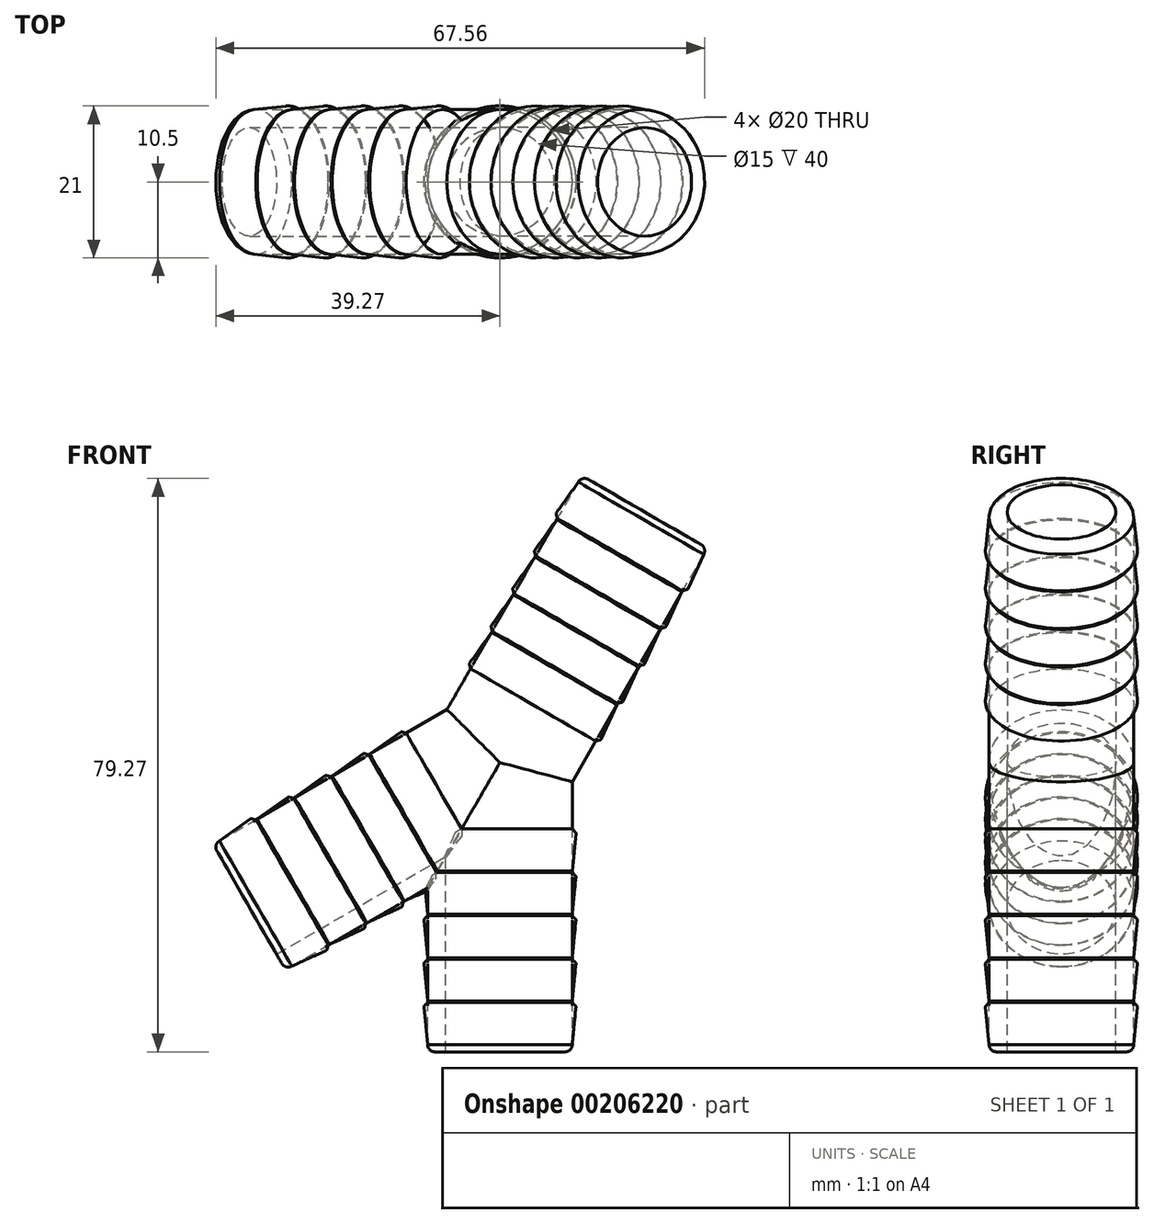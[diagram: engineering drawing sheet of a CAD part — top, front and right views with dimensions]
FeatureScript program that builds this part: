
annotation { "Feature Type Name" : "Feature", "Feature Type Description" : "" }
export const myFeature = defineFeature(function(context is Context, id is Id, definition is map)
    precondition{}
    {
        {
            var Q0;
            Q0=qCreatedBy(makeId("Front.planeOp"),FACE);
            var sketch = newSketch(context, id + "F4", { "sketchPlane" : qUnion([Q0])});
            skLineSegment(sketch, "E0.bottom", {"start": v(-10, 0) * mm, "end": v(10, 0) * mm});
            skLineSegment(sketch, "E0.top", {"start": v(-9, -40) * mm, "end": v(9, -40) * mm});
            skLineSegment(sketch, "E0.left", {"start": v(-10, 0) * mm, "end": v(-10, -39) * mm});
            skLineSegment(sketch, "E0.right", {"start": v(10, 0) * mm, "end": v(10, -39) * mm});
            skCircle(sketch, "E1", {"center": v(0, 0) * mm, "radius": 10 * mm});
            skLineSegment(sketch, "E2", {"start": v(0, 0) * mm, "end": v(0, -82.88) * mm});
            skPoint(sketch, "E3.visualSharp", {"position": v(-10, -40) * mm});
            skArc(sketch, "E3.filletArc", {"start": v(-10, -39) * mm, "mid": v(-9.7, -39.7) * mm, "end": v(-9, -40) * mm});
            skPoint(sketch, "E4.visualSharp", {"position": v(10, -40) * mm});
            skArc(sketch, "E4.filletArc", {"start": v(9, -40) * mm, "mid": v(9.7, -39.7) * mm, "end": v(10, -39) * mm});
            skArc(sketch, "E5", {"start": v(-10.43, -33.62) * mm, "mid": v(-10.49, -33.71) * mm, "end": v(-10.5, -33.82) * mm});
            skLineSegment(sketch, "E6", {"start": v(-10.5, -33.82) * mm, "end": v(-10, -39) * mm});
            skLineSegment(sketch, "E7", {"start": v(-10.43, -33.62) * mm, "end": v(-10, -33.2) * mm});
            skLineSegment(sketch, "E8.0.1.0", {"start": v(-10.43, -27.62) * mm, "end": v(-10, -27.2) * mm});
            skArc(sketch, "E8.0.1.1", {"start": v(-10.43, -27.62) * mm, "mid": v(-10.49, -27.71) * mm, "end": v(-10.5, -27.82) * mm});
            skLineSegment(sketch, "E8.0.1.2", {"start": v(-10.5, -27.82) * mm, "end": v(-10, -33) * mm});
            skLineSegment(sketch, "E8.0.2.0", {"start": v(-10.43, -21.62) * mm, "end": v(-10, -21.2) * mm});
            skArc(sketch, "E8.0.2.1", {"start": v(-10.43, -21.62) * mm, "mid": v(-10.49, -21.71) * mm, "end": v(-10.5, -21.82) * mm});
            skLineSegment(sketch, "E8.0.2.2", {"start": v(-10.5, -21.82) * mm, "end": v(-10, -27) * mm});
            skLineSegment(sketch, "E8.0.3.0", {"start": v(-10.43, -15.62) * mm, "end": v(-10, -15.2) * mm});
            skArc(sketch, "E8.0.3.1", {"start": v(-10.43, -15.62) * mm, "mid": v(-10.49, -15.71) * mm, "end": v(-10.5, -15.82) * mm});
            skLineSegment(sketch, "E8.0.3.2", {"start": v(-10.5, -15.82) * mm, "end": v(-10, -21) * mm});
            skLineSegment(sketch, "E8.0.4.0", {"start": v(-10.43, -9.62) * mm, "end": v(-10, -9.2) * mm});
            skArc(sketch, "E8.0.4.1", {"start": v(-10.43, -9.62) * mm, "mid": v(-10.49, -9.71) * mm, "end": v(-10.5, -9.82) * mm});
            skLineSegment(sketch, "E8.0.4.2", {"start": v(-10.5, -9.82) * mm, "end": v(-10, -15) * mm});
            skLineSegment(sketch, "E8.direction1", {"start": v(-10.5, -33.82) * mm, "end": v(14.5, -33.82) * mm, "construction": true});
            skLineSegment(sketch, "E8.direction2", {"start": v(-10.5, -33.82) * mm, "end": v(-10.5, -27.82) * mm, "construction": true});
            skSolve(sketch);
        }
        {
            var Q0;
            {var subQ11=sQuery(id+"F4.wireOp",EDGE,"E3.filletArc");Q0=makeQuery(id+"F4.imprint","IMPRINT",FACE,{"disambiguationData":[TD([[makeQuery(id+"F4.imprint","IMPRINT",EDGE,{"derivedFrom":subQ11}),1.0]])]});}
            var Q1;
            {var subQ1=sQuery(id+"F4.wireOp",EDGE,"E0.bottom");var subQ3=sQuery(id+"F4.wireOp",EDGE,"E2");var subQ4=makeQuery(id+"F4.imprint","INTERSECT",VERTEX,{"derivedFrom":[subQ1,subQ3]});Q1=makeQuery(id+"F4.imprint","IMPRINT",FACE,{"disambiguationData":[TD([[makeQuery(id+"F4.imprint","IMPRINT",EDGE,{"disambiguationData":[TD([[subQ4,-1.0]])],"derivedFrom":subQ3}),-1.0]])]});}
            var Q2;
            Q2=sQuery(id+"F4.wireOp",EDGE,"E2");
            revolve(context, id + "F0", {"entities" : qUnion([Q0, Q1]), "axis" : qUnion([Q2]), "revolveType" : RevolveType.FULL});
        }
        {
            var Q0;
            Q0=makeQuery(id+"F6e7yGGuFcoaENt3P_0.opExtrude","SWEPT_BODY",BODY,{"disambiguationData":[OSD([sQuery(id+"F4.wireOp",EDGE,"E0.bottom"),sQuery(id+"F4.wireOp",EDGE,"E0.top"),sQuery(id+"F4.wireOp",EDGE,"E0.left"),sQuery(id+"F4.wireOp",EDGE,"E0.right")])]});
            var Q1;
            Q1=makeQuery(id+"F0.opRevolve","SWEPT_BODY",BODY,{"disambiguationData":[OSD([sQuery(id+"F4.wireOp",EDGE,"E0.bottom"),sQuery(id+"F4.wireOp",EDGE,"E0.top"),sQuery(id+"F4.wireOp",EDGE,"E0.left"),sQuery(id+"F4.wireOp",EDGE,"E2")])]});
            var Q2;
            Q2=sQuery(id+"F4.wireOp",EDGE,"E1");
            circularPattern(context, id + "F1", {"operationType" : NewBodyOperationType.ADD, "entities" : qUnion([Q0, Q1]), "axis" : qUnion([Q2]), "angle" : 300 * degree, "instanceCount" : 3, "equalSpace" : true});
        }
        {
            var Q0;
            {var subQ0=sQuery(id+"F4.wireOp",EDGE,"E8.0.4.0");Q0=makeQuery(id+"F4.imprint","IMPRINT",FACE,{"disambiguationData":[TD([[makeQuery(id+"F4.imprint","IMPRINT",EDGE,{"derivedFrom":subQ0}),-1.0]])]});}
            var Q1;
            {var subQ0=sQuery(id+"F4.wireOp",EDGE,"E8.0.3.0");Q1=makeQuery(id+"F4.imprint","IMPRINT",FACE,{"disambiguationData":[TD([[makeQuery(id+"F4.imprint","IMPRINT",EDGE,{"derivedFrom":subQ0}),-1.0]])]});}
            var Q2;
            {var subQ0=sQuery(id+"F4.wireOp",EDGE,"E8.0.2.0");Q2=makeQuery(id+"F4.imprint","IMPRINT",FACE,{"disambiguationData":[TD([[makeQuery(id+"F4.imprint","IMPRINT",EDGE,{"derivedFrom":subQ0}),-1.0]])]});}
            var Q3;
            {var subQ0=sQuery(id+"F4.wireOp",EDGE,"E8.0.1.0");Q3=makeQuery(id+"F4.imprint","IMPRINT",FACE,{"disambiguationData":[TD([[makeQuery(id+"F4.imprint","IMPRINT",EDGE,{"derivedFrom":subQ0}),-1.0]])]});}
            var Q4;
            Q4=makeQuery(id+"F4.imprint","IMPRINT",FACE,{"disambiguationData":[TD([[makeQuery(id+"F4.imprint","IMPRINT",EDGE,{"derivedFrom":sQuery(id+"F4.wireOp",EDGE,"E5")}),1.0]])]});
            var Q5;
            Q5=sQuery(id+"F4.wireOp",EDGE,"E2");
            revolve(context, id + "F5", {"entities" : qUnion([Q0, Q1, Q2, Q3, Q4]), "axis" : qUnion([Q5]), "revolveType" : RevolveType.FULL});
        }
        {
            var Q0;
            Q0=makeQuery(id+"F5.opRevolve","SWEPT_BODY",BODY,{"disambiguationData":[OSD([sQuery(id+"F4.wireOp",EDGE,"E0.left"),sQuery(id+"F4.wireOp",EDGE,"E8.0.2.0"),sQuery(id+"F4.wireOp",EDGE,"E8.0.2.1"),sQuery(id+"F4.wireOp",EDGE,"E8.0.2.2")])]});
            var Q1;
            Q1=makeQuery(id+"F5.opRevolve","SWEPT_BODY",BODY,{"disambiguationData":[OSD([sQuery(id+"F4.wireOp",EDGE,"E0.left"),sQuery(id+"F4.wireOp",EDGE,"E5"),sQuery(id+"F4.wireOp",EDGE,"E6"),sQuery(id+"F4.wireOp",EDGE,"E7")])]});
            var Q2;
            Q2=makeQuery(id+"F5.opRevolve","SWEPT_BODY",BODY,{"disambiguationData":[OSD([sQuery(id+"F4.wireOp",EDGE,"E0.left"),sQuery(id+"F4.wireOp",EDGE,"E8.0.1.0"),sQuery(id+"F4.wireOp",EDGE,"E8.0.1.1"),sQuery(id+"F4.wireOp",EDGE,"E8.0.1.2")])]});
            var Q3;
            Q3=makeQuery(id+"F5.opRevolve","SWEPT_BODY",BODY,{"disambiguationData":[OSD([sQuery(id+"F4.wireOp",EDGE,"E0.left"),sQuery(id+"F4.wireOp",EDGE,"E8.0.3.0"),sQuery(id+"F4.wireOp",EDGE,"E8.0.3.1"),sQuery(id+"F4.wireOp",EDGE,"E8.0.3.2")])]});
            var Q4;
            Q4=makeQuery(id+"F5.opRevolve","SWEPT_BODY",BODY,{"disambiguationData":[OSD([sQuery(id+"F4.wireOp",EDGE,"E0.left"),sQuery(id+"F4.wireOp",EDGE,"E8.0.4.0"),sQuery(id+"F4.wireOp",EDGE,"E8.0.4.1"),sQuery(id+"F4.wireOp",EDGE,"E8.0.4.2")])]});
            var Q5;
            Q5=sQuery(id+"F4.wireOp",EDGE,"E1");
            circularPattern(context, id + "F2", {"entities" : qUnion([Q0, Q1, Q2, Q3, Q4]), "axis" : qUnion([Q5]), "angle" : 300 * degree, "instanceCount" : 3, "equalSpace" : true});
        }
        {
            var Q0;
            Q0=makeQuery(id+"F0.opRevolve","SWEPT_BODY",BODY,{"disambiguationData":[OSD([sQuery(id+"F4.wireOp",EDGE,"E0.bottom"),sQuery(id+"F4.wireOp",EDGE,"E0.top"),sQuery(id+"F4.wireOp",EDGE,"E0.left"),sQuery(id+"F4.wireOp",EDGE,"E2"),sQuery(id+"F4.wireOp",EDGE,"E3.filletArc")])]});
            var Q1;
            Q1=makeQuery(id+"F2.opPattern","COPY",BODY,{"derivedFrom":makeQuery(id+"F5.opRevolve","SWEPT_BODY",BODY,{"disambiguationData":[OSD([sQuery(id+"F4.wireOp",EDGE,"E0.left"),sQuery(id+"F4.wireOp",EDGE,"E8.0.4.0"),sQuery(id+"F4.wireOp",EDGE,"E8.0.4.1"),sQuery(id+"F4.wireOp",EDGE,"E8.0.4.2")])]}),"instanceName":"2"});
            var Q2;
            Q2=makeQuery(id+"F5.opRevolve","SWEPT_BODY",BODY,{"disambiguationData":[OSD([sQuery(id+"F4.wireOp",EDGE,"E0.left"),sQuery(id+"F4.wireOp",EDGE,"E8.0.4.0"),sQuery(id+"F4.wireOp",EDGE,"E8.0.4.1"),sQuery(id+"F4.wireOp",EDGE,"E8.0.4.2")])]});
            var Q3;
            Q3=makeQuery(id+"F5.opRevolve","SWEPT_BODY",BODY,{"disambiguationData":[OSD([sQuery(id+"F4.wireOp",EDGE,"E0.left"),sQuery(id+"F4.wireOp",EDGE,"E8.0.3.0"),sQuery(id+"F4.wireOp",EDGE,"E8.0.3.1"),sQuery(id+"F4.wireOp",EDGE,"E8.0.3.2")])]});
            var Q4;
            Q4=makeQuery(id+"F2.opPattern","COPY",BODY,{"derivedFrom":makeQuery(id+"F5.opRevolve","SWEPT_BODY",BODY,{"disambiguationData":[OSD([sQuery(id+"F4.wireOp",EDGE,"E0.left"),sQuery(id+"F4.wireOp",EDGE,"E8.0.3.0"),sQuery(id+"F4.wireOp",EDGE,"E8.0.3.1"),sQuery(id+"F4.wireOp",EDGE,"E8.0.3.2")])]}),"instanceName":"2"});
            booleanBodies(context, id + "F3", {"operationType" : BooleanOperationType.SUBTRACTION, "tools" : qUnion([Q0]), "targets" : qUnion([Q1, Q2, Q3, Q4]), "keepTools" : true});
        }
        {
            var Q0;
            Q0=makeQuery(id+"F0.opRevolve","SWEPT_FACE",FACE,{"disambiguationData":[OSD([sQuery(id+"F4.wireOp",EDGE,"E0.top")])]});
            var Q1;
            Q1=makeQuery(id+"F1.opPattern","COPY",FACE,{"derivedFrom":makeQuery(id+"F0.opRevolve","SWEPT_FACE",FACE,{"disambiguationData":[OSD([sQuery(id+"F4.wireOp",EDGE,"E0.top")])]}),"instanceName":"2"});
            var Q2;
            Q2=makeQuery(id+"F1.opPattern","COPY",FACE,{"derivedFrom":makeQuery(id+"F0.opRevolve","SWEPT_FACE",FACE,{"disambiguationData":[OSD([sQuery(id+"F4.wireOp",EDGE,"E0.top")])]}),"instanceName":"1"});
            shell(context, id + "F6", {"entities" : qUnion([Q0, Q1, Q2]), "thickness" : 2.5 * mm});
        }
    });
